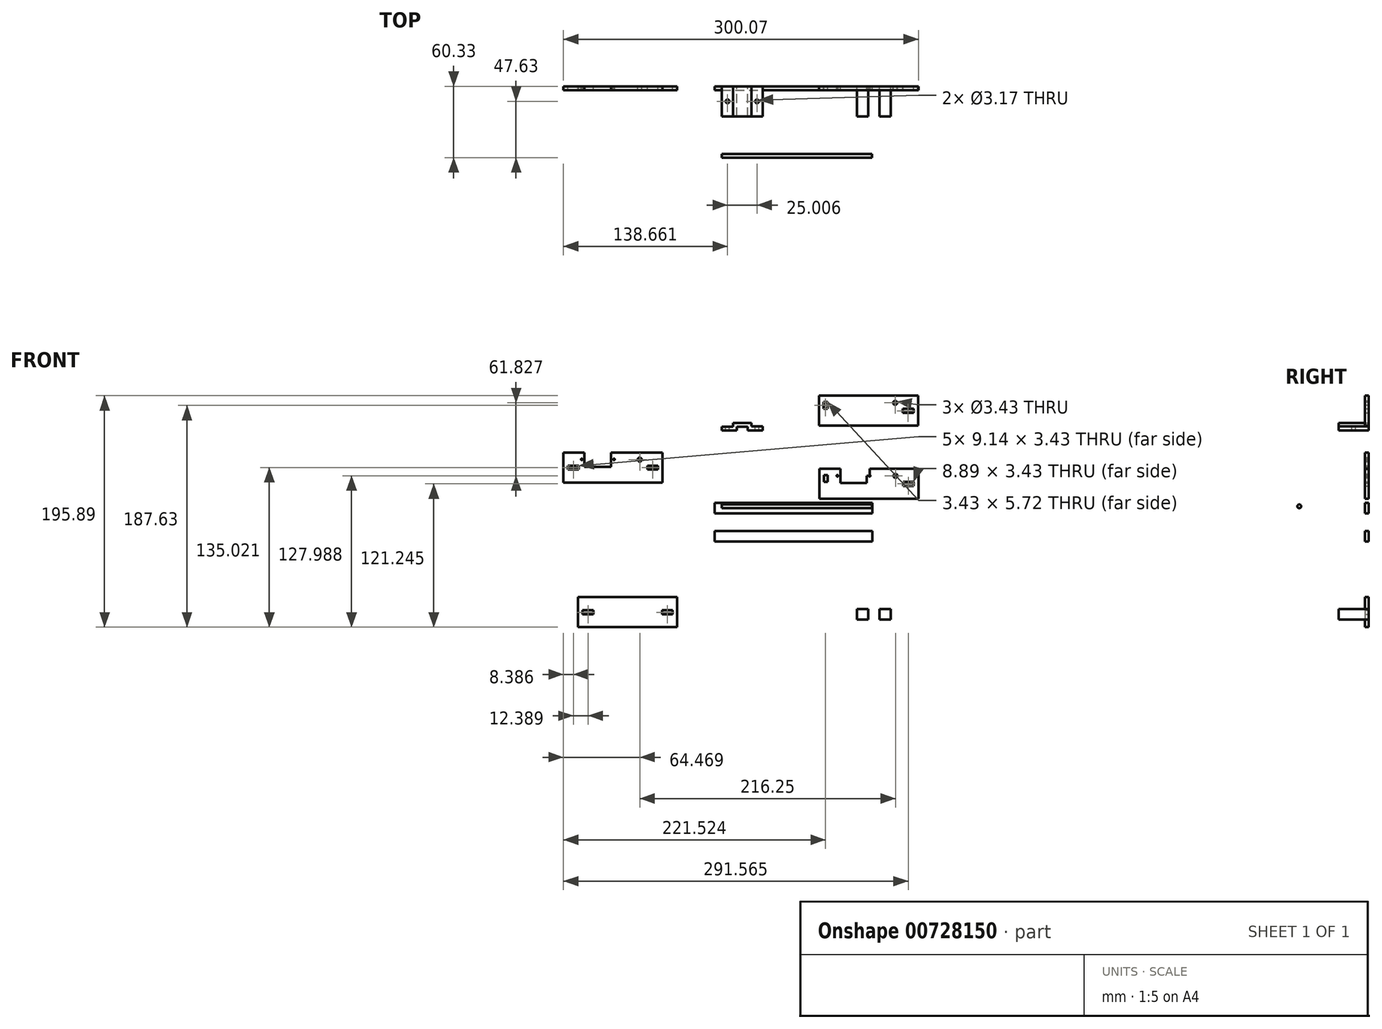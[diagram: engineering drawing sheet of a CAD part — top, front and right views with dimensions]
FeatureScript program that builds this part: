
annotation { "Feature Type Name" : "Feature", "Feature Type Description" : "" }
export const myFeature = defineFeature(function(context is Context, id is Id, definition is map)
    precondition{}
    {
        {
            var Q0;
            Q0=qCreatedBy(makeId("Front.planeOp"),FACE);
            var sketch = newSketch(context, id + "F0", { "sketchPlane" : qUnion([Q0])});
            skLineSegment(sketch, "E0.bottom", {"start": v(-44.59, 14.54) * mm, "end": v(39.23, 14.54) * mm});
            skLineSegment(sketch, "E0.top", {"start": v(-44.59, -10.86) * mm, "end": v(39.23, -10.86) * mm});
            skLineSegment(sketch, "E0.left", {"start": v(-44.59, 14.54) * mm, "end": v(-44.59, -10.86) * mm});
            skLineSegment(sketch, "E0.right", {"start": v(39.23, 14.54) * mm, "end": v(39.23, -10.86) * mm});
            skLineSegment(sketch, "E1.bottom", {"start": v(-28.47, -10.86) * mm, "end": v(-5.43, -10.86) * mm});
            skLineSegment(sketch, "E2.bottom", {"start": v(-133.06, -14.32) * mm, "end": v(0.29, -14.32) * mm});
            skLineSegment(sketch, "E2.top", {"start": v(-133.06, -23.21) * mm, "end": v(0.29, -23.21) * mm});
            skLineSegment(sketch, "E2.left", {"start": v(-133.06, -14.32) * mm, "end": v(-133.06, -23.21) * mm});
            skLineSegment(sketch, "E2.right", {"start": v(0.29, -14.32) * mm, "end": v(0.29, -23.21) * mm});
            skLineSegment(sketch, "E3.bottom", {"start": v(-133.06, -38.27) * mm, "end": v(0.29, -38.27) * mm});
            skLineSegment(sketch, "E3.top", {"start": v(-133.06, -47.16) * mm, "end": v(0.29, -47.16) * mm});
            skLineSegment(sketch, "E3.left", {"start": v(-133.06, -38.27) * mm, "end": v(-133.06, -47.16) * mm});
            skLineSegment(sketch, "E3.right", {"start": v(0.29, -38.27) * mm, "end": v(0.29, -47.16) * mm});
            skLineSegment(sketch, "E4.bottom", {"start": v(-44.84, 76.36) * mm, "end": v(38.98, 76.36) * mm});
            skLineSegment(sketch, "E4.top", {"start": v(-44.84, 50.96) * mm, "end": v(38.98, 50.96) * mm});
            skLineSegment(sketch, "E4.left", {"start": v(-44.84, 76.36) * mm, "end": v(-44.84, 50.96) * mm});
            skLineSegment(sketch, "E4.right", {"start": v(38.98, 76.36) * mm, "end": v(38.98, 50.96) * mm});
            skLineSegment(sketch, "E5", {"start": v(-40.78, 14.54) * mm, "end": v(-40.78, 3.43) * mm});
            skLineSegment(sketch, "E6", {"start": v(-41.03, 76.36) * mm, "end": v(-41.03, 65.24) * mm});
            skLineSegment(sketch, "E7.bottom", {"start": v(-40.78, 3.43) * mm, "end": v(-31.89, 3.43) * mm});
            skLineSegment(sketch, "E7.top", {"start": v(-40.78, 0) * mm, "end": v(-31.89, 0) * mm});
            skLineSegment(sketch, "E7.left", {"start": v(-40.78, 3.43) * mm, "end": v(-40.78, 0) * mm});
            skLineSegment(sketch, "E7.right", {"start": v(-31.89, 3.43) * mm, "end": v(-31.89, 0) * mm});
            skLineSegment(sketch, "E8.bottom", {"start": v(-41.03, 65.24) * mm, "end": v(-31.89, 65.24) * mm});
            skLineSegment(sketch, "E8.top", {"start": v(-41.03, 61.81) * mm, "end": v(-31.89, 61.81) * mm});
            skLineSegment(sketch, "E8.left", {"start": v(-41.03, 65.24) * mm, "end": v(-41.03, 61.81) * mm});
            skLineSegment(sketch, "E8.right", {"start": v(-31.89, 65.24) * mm, "end": v(-31.89, 61.81) * mm});
            skLineSegment(sketch, "E9.bottom", {"start": v(-44.84, 76.36) * mm, "end": v(-41.03, 76.36) * mm});
            skLineSegment(sketch, "E9.top", {"start": v(-44.84, 76.36) * mm, "end": v(-41.03, 76.36) * mm});
            skLineSegment(sketch, "E9.left", {"start": v(-44.84, 76.36) * mm, "end": v(-44.84, 76.36) * mm});
            skLineSegment(sketch, "E9.right", {"start": v(-41.03, 76.36) * mm, "end": v(-41.03, 76.36) * mm});
            skLineSegment(sketch, "E10", {"start": v(35.17, 76.36) * mm, "end": v(35.17, 65.24) * mm});
            skPoint(sketch, "E11.oppositeSnap0", {"position": v(-36.46, 61.81) * mm});
            skLineSegment(sketch, "E11.bottom", {"start": v(35.17, 65.24) * mm, "end": v(26.03, 65.24) * mm});
            skLineSegment(sketch, "E11.top", {"start": v(35.17, 61.81) * mm, "end": v(26.03, 61.81) * mm});
            skLineSegment(sketch, "E11.left", {"start": v(35.17, 65.24) * mm, "end": v(35.17, 61.81) * mm});
            skLineSegment(sketch, "E11.right", {"start": v(26.03, 65.24) * mm, "end": v(26.03, 61.81) * mm});
            skLineSegment(sketch, "E12.left", {"start": v(35.42, 0.25) * mm, "end": v(35.17, 0) * mm});
            skLineSegment(sketch, "E13", {"start": v(35.42, 0.25) * mm, "end": v(35.42, -10.86) * mm});
            skLineSegment(sketch, "E14.bottom", {"start": v(35.17, 0) * mm, "end": v(26.28, 0) * mm});
            skLineSegment(sketch, "E14.top", {"start": v(35.17, 3.43) * mm, "end": v(26.28, 3.43) * mm});
            skLineSegment(sketch, "E14.left", {"start": v(35.17, 0) * mm, "end": v(35.17, 3.43) * mm});
            skLineSegment(sketch, "E14.right", {"start": v(26.28, 0) * mm, "end": v(26.28, 3.43) * mm});
            skLineSegment(sketch, "E15.bottom", {"start": v(-26.8, 14.54) * mm, "end": v(-4.33, 14.54) * mm});
            skLineSegment(sketch, "E15.top", {"start": v(-26.8, 2.37) * mm, "end": v(-4.33, 2.37) * mm});
            skLineSegment(sketch, "E15.left", {"start": v(-26.8, 14.54) * mm, "end": v(-26.8, 2.37) * mm});
            skLineSegment(sketch, "E15.right", {"start": v(-4.33, 14.54) * mm, "end": v(-4.33, 2.37) * mm});
            skLineSegment(sketch, "E16", {"start": v(-15.57, 14.54) * mm, "end": v(9.83, 14.54) * mm});
            skLineSegment(sketch, "E17", {"start": v(-44.84, 76.36) * mm, "end": v(9.6, 76.36) * mm});
            skLineSegment(sketch, "E18.bottom", {"start": v(-126.95, 53.3) * mm, "end": v(-92.41, 53.3) * mm});
            skLineSegment(sketch, "E18.top", {"start": v(-126.95, 46.96) * mm, "end": v(-92.41, 46.96) * mm});
            skLineSegment(sketch, "E18.left", {"start": v(-126.95, 53.3) * mm, "end": v(-126.95, 46.96) * mm});
            skLineSegment(sketch, "E18.right", {"start": v(-92.41, 53.3) * mm, "end": v(-92.41, 46.96) * mm});
            skLineSegment(sketch, "E19", {"start": v(-114.25, 46.96) * mm, "end": v(-114.25, 50.13) * mm});
            skLineSegment(sketch, "E20", {"start": v(-114.25, 50.13) * mm, "end": v(-105.11, 50.13) * mm});
            skLineSegment(sketch, "E21", {"start": v(-105.11, 50.13) * mm, "end": v(-105.11, 46.96) * mm});
            skLineSegment(sketch, "E22", {"start": v(-126.95, 50.13) * mm, "end": v(-117.43, 50.13) * mm});
            skLineSegment(sketch, "E23", {"start": v(-117.43, 50.13) * mm, "end": v(-117.43, 53.3) * mm});
            skLineSegment(sketch, "E24", {"start": v(-101.94, 53.3) * mm, "end": v(-101.94, 50.36) * mm});
            skLineSegment(sketch, "E25", {"start": v(-101.94, 50.36) * mm, "end": v(-92.41, 50.36) * mm});
            skLineSegment(sketch, "E26", {"start": v(-29.19, 14.54) * mm, "end": v(-29.19, 8.6) * mm});
            skLineSegment(sketch, "E27", {"start": v(-29.19, 8.6) * mm, "end": v(-26.8, 8.6) * mm});
            skLineSegment(sketch, "E28.bottom", {"start": v(-4.33, 14.54) * mm, "end": v(-1.94, 14.54) * mm});
            skLineSegment(sketch, "E28.left", {"start": v(-4.33, 14.54) * mm, "end": v(-4.33, 8.59) * mm});
            skLineSegment(sketch, "E28.right", {"start": v(-1.94, 14.54) * mm, "end": v(-1.94, 8.59) * mm});
            skCircle(sketch, "E29", {"center": v(-29.19, 8.6) * mm, "radius": 0.64 * mm});
            skCircle(sketch, "E30", {"center": v(-1.94, 8.59) * mm, "radius": 0.64 * mm});
            skLineSegment(sketch, "E31.bottom", {"start": v(-260.84, 28.33) * mm, "end": v(-177.02, 28.33) * mm});
            skLineSegment(sketch, "E31.top", {"start": v(-260.84, 2.93) * mm, "end": v(-177.02, 2.93) * mm});
            skLineSegment(sketch, "E31.left", {"start": v(-260.84, 28.33) * mm, "end": v(-260.84, 2.93) * mm});
            skLineSegment(sketch, "E31.right", {"start": v(-177.02, 28.33) * mm, "end": v(-177.02, 2.93) * mm});
            skLineSegment(sketch, "E32", {"start": v(-257.03, 28.33) * mm, "end": v(-180.83, 28.33) * mm});
            skLineSegment(sketch, "E33.bottom", {"start": v(-257.03, 17.2) * mm, "end": v(-247.88, 17.2) * mm});
            skLineSegment(sketch, "E33.top", {"start": v(-257.03, 13.78) * mm, "end": v(-247.88, 13.78) * mm});
            skLineSegment(sketch, "E33.left", {"start": v(-257.03, 17.2) * mm, "end": v(-257.03, 13.78) * mm});
            skLineSegment(sketch, "E33.right", {"start": v(-247.88, 17.2) * mm, "end": v(-247.88, 13.78) * mm});
            skLineSegment(sketch, "E34.bottom", {"start": v(-180.83, 17.2) * mm, "end": v(-189.97, 17.2) * mm});
            skLineSegment(sketch, "E34.top", {"start": v(-180.83, 13.78) * mm, "end": v(-189.97, 13.78) * mm});
            skLineSegment(sketch, "E34.left", {"start": v(-180.83, 17.2) * mm, "end": v(-180.83, 13.78) * mm});
            skLineSegment(sketch, "E34.right", {"start": v(-189.97, 17.2) * mm, "end": v(-189.97, 13.78) * mm});
            skLineSegment(sketch, "E35", {"start": v(-10.6, 8.46) * mm, "end": v(19.88, 8.46) * mm});
            skLineSegment(sketch, "E36", {"start": v(9.6, 76.36) * mm, "end": v(9.6, 70.26) * mm});
            skLineSegment(sketch, "E37.bottom", {"start": v(-260.84, 28.33) * mm, "end": v(-206.4, 28.33) * mm});
            skLineSegment(sketch, "E37.left", {"start": v(-260.84, 28.33) * mm, "end": v(-260.84, 22.23) * mm});
            skLineSegment(sketch, "E38", {"start": v(-260.84, 28.33) * mm, "end": v(-243.06, 28.33) * mm});
            skLineSegment(sketch, "E39.bottom", {"start": v(-243.06, 28.33) * mm, "end": v(-220.58, 28.33) * mm});
            skLineSegment(sketch, "E39.top", {"start": v(-243.06, 16.16) * mm, "end": v(-220.58, 16.16) * mm});
            skLineSegment(sketch, "E39.left", {"start": v(-243.06, 28.33) * mm, "end": v(-243.06, 16.16) * mm});
            skLineSegment(sketch, "E39.right", {"start": v(-220.58, 28.33) * mm, "end": v(-220.58, 16.16) * mm});
            skCircle(sketch, "E40", {"center": v(-245.44, 22.39) * mm, "radius": 0.64 * mm});
            skCircle(sketch, "E41", {"center": v(-218.19, 22.39) * mm, "radius": 0.64 * mm});
            skLineSegment(sketch, "E42.bottom", {"start": v(-248.45, -94.13) * mm, "end": v(-164.63, -94.13) * mm});
            skLineSegment(sketch, "E42.top", {"start": v(-248.45, -119.53) * mm, "end": v(-164.63, -119.53) * mm});
            skLineSegment(sketch, "E42.left", {"start": v(-248.45, -94.13) * mm, "end": v(-248.45, -119.53) * mm});
            skLineSegment(sketch, "E42.right", {"start": v(-164.63, -94.13) * mm, "end": v(-164.63, -119.53) * mm});
            skLineSegment(sketch, "E43", {"start": v(-248.45, -94.13) * mm, "end": v(-244.64, -94.13) * mm});
            skLineSegment(sketch, "E44", {"start": v(-164.63, -94.13) * mm, "end": v(-168.44, -94.13) * mm});
            skLineSegment(sketch, "E45", {"start": v(-244.64, -94.13) * mm, "end": v(-244.64, -105.25) * mm});
            skLineSegment(sketch, "E46", {"start": v(-168.44, -94.13) * mm, "end": v(-168.44, -105.25) * mm});
            skLineSegment(sketch, "E47.bottom", {"start": v(-244.64, -105.25) * mm, "end": v(-235.5, -105.25) * mm});
            skLineSegment(sketch, "E47.top", {"start": v(-244.64, -108.68) * mm, "end": v(-235.5, -108.68) * mm});
            skLineSegment(sketch, "E47.left", {"start": v(-244.64, -105.25) * mm, "end": v(-244.64, -108.68) * mm});
            skLineSegment(sketch, "E47.right", {"start": v(-235.5, -105.25) * mm, "end": v(-235.5, -108.68) * mm});
            skLineSegment(sketch, "E48.bottom", {"start": v(-168.44, -105.25) * mm, "end": v(-177.58, -105.25) * mm});
            skLineSegment(sketch, "E48.top", {"start": v(-168.44, -108.68) * mm, "end": v(-177.58, -108.68) * mm});
            skLineSegment(sketch, "E48.left", {"start": v(-168.44, -105.25) * mm, "end": v(-168.44, -108.68) * mm});
            skLineSegment(sketch, "E48.right", {"start": v(-177.58, -105.25) * mm, "end": v(-177.58, -108.68) * mm});
            skLineSegment(sketch, "E49.bottom", {"start": v(-98.52, -99.6) * mm, "end": v(-63.97, -99.6) * mm});
            skLineSegment(sketch, "E49.top", {"start": v(-98.52, -106.2) * mm, "end": v(-63.97, -106.2) * mm});
            skLineSegment(sketch, "E49.left", {"start": v(-98.52, -99.6) * mm, "end": v(-98.52, -106.2) * mm});
            skLineSegment(sketch, "E49.right", {"start": v(-63.97, -99.6) * mm, "end": v(-63.97, -106.2) * mm});
            skLineSegment(sketch, "E50.bottom", {"start": v(-98.52, -99.6) * mm, "end": v(-89, -99.6) * mm});
            skLineSegment(sketch, "E50.top", {"start": v(-98.52, -97.05) * mm, "end": v(-89, -97.05) * mm});
            skLineSegment(sketch, "E50.left", {"start": v(-98.52, -97.05) * mm, "end": v(-98.52, -99.6) * mm});
            skLineSegment(sketch, "E50.right", {"start": v(-89, -97.05) * mm, "end": v(-89, -99.6) * mm});
            skLineSegment(sketch, "E51.bottom", {"start": v(-63.97, -99.6) * mm, "end": v(-73.5, -99.6) * mm});
            skLineSegment(sketch, "E51.top", {"start": v(-63.97, -102.77) * mm, "end": v(-73.5, -102.77) * mm});
            skLineSegment(sketch, "E51.left", {"start": v(-63.97, -99.6) * mm, "end": v(-63.97, -102.77) * mm});
            skLineSegment(sketch, "E51.right", {"start": v(-73.5, -99.6) * mm, "end": v(-73.5, -102.77) * mm});
            skLineSegment(sketch, "E52.bottom", {"start": v(-85.82, -106.2) * mm, "end": v(-76.67, -106.2) * mm});
            skLineSegment(sketch, "E52.top", {"start": v(-85.82, -97.05) * mm, "end": v(-76.67, -97.05) * mm});
            skLineSegment(sketch, "E52.left", {"start": v(-85.82, -106.2) * mm, "end": v(-85.82, -97.05) * mm});
            skLineSegment(sketch, "E52.right", {"start": v(-76.67, -106.2) * mm, "end": v(-76.67, -97.05) * mm});
            skLineSegment(sketch, "E53", {"start": v(-10.6, 14.54) * mm, "end": v(-4.33, 14.54) * mm});
            skLineSegment(sketch, "E54", {"start": v(-10.6, 14.54) * mm, "end": v(-10.6, 8.46) * mm});
            skCircle(sketch, "E55", {"center": v(19.88, 8.46) * mm, "radius": 1.71 * mm});
            skLineSegment(sketch, "E56", {"start": v(-226.85, 28.33) * mm, "end": v(-220.58, 28.33) * mm});
            skCircle(sketch, "E57", {"center": v(-196.37, 22.23) * mm, "radius": 1.71 * mm});
            skLineSegment(sketch, "E58.bottom", {"start": v(35.17, 61.81) * mm, "end": v(31.74, 61.81) * mm});
            skLineSegment(sketch, "E58.top", {"start": v(35.17, 70.96) * mm, "end": v(31.74, 70.96) * mm});
            skLineSegment(sketch, "E58.left", {"start": v(35.17, 61.81) * mm, "end": v(35.17, 70.96) * mm});
            skLineSegment(sketch, "E58.right", {"start": v(31.74, 61.81) * mm, "end": v(31.74, 70.96) * mm});
            skLineSegment(sketch, "E59.bottom", {"start": v(-12.7, -104.07) * mm, "end": v(15.88, -104.07) * mm});
            skLineSegment(sketch, "E59.top", {"start": v(-12.7, -116.14) * mm, "end": v(15.88, -116.14) * mm});
            skLineSegment(sketch, "E59.left", {"start": v(-12.7, -104.07) * mm, "end": v(-12.7, -116.14) * mm});
            skLineSegment(sketch, "E59.right", {"start": v(15.88, -104.07) * mm, "end": v(15.88, -116.14) * mm});
            skLineSegment(sketch, "E60.bottom", {"start": v(15.93, -104.07) * mm, "end": v(15.88, -104.07) * mm});
            skLineSegment(sketch, "E60.top", {"start": v(15.91, -101) * mm, "end": v(15.88, -101) * mm});
            skLineSegment(sketch, "E61.bottom", {"start": v(0, -116.14) * mm, "end": v(3.18, -116.14) * mm});
            skLineSegment(sketch, "E61.top", {"start": v(0, -107.25) * mm, "end": v(3.17, -107.25) * mm});
            skLineSegment(sketch, "E61.left", {"start": v(0, -116.14) * mm, "end": v(0, -107.25) * mm});
            skLineSegment(sketch, "E61.right", {"start": v(3.18, -116.14) * mm, "end": v(3.17, -107.25) * mm});
            skLineSegment(sketch, "E62.bottom", {"start": v(-12.7, -104.07) * mm, "end": v(-3.18, -104.07) * mm});
            skLineSegment(sketch, "E62.top", {"start": v(-12.7, -112.96) * mm, "end": v(-3.18, -112.96) * mm});
            skLineSegment(sketch, "E62.left", {"start": v(-12.7, -104.07) * mm, "end": v(-12.7, -112.96) * mm});
            skLineSegment(sketch, "E62.right", {"start": v(-3.18, -104.07) * mm, "end": v(-3.18, -112.96) * mm});
            skLineSegment(sketch, "E63.bottom", {"start": v(15.93, -104.07) * mm, "end": v(6.4, -104.07) * mm});
            skLineSegment(sketch, "E63.top", {"start": v(15.93, -112.97) * mm, "end": v(6.4, -112.97) * mm});
            skLineSegment(sketch, "E63.left", {"start": v(15.93, -104.07) * mm, "end": v(15.93, -112.97) * mm});
            skLineSegment(sketch, "E63.right", {"start": v(6.4, -104.07) * mm, "end": v(6.4, -112.97) * mm});
            skLineSegment(sketch, "E64", {"start": v(-44.84, 76.36) * mm, "end": v(19.62, 76.36) * mm});
            skLineSegment(sketch, "E65", {"start": v(19.62, 76.36) * mm, "end": v(19.62, 70.28) * mm});
            skCircle(sketch, "E66", {"center": v(19.62, 70.28) * mm, "radius": 1.71 * mm});
            skLineSegment(sketch, "E67.bottom", {"start": v(-40.78, 0) * mm, "end": v(-37.35, 0) * mm});
            skLineSegment(sketch, "E67.top", {"start": v(-40.78, 9.14) * mm, "end": v(-37.35, 9.14) * mm});
            skLineSegment(sketch, "E67.left", {"start": v(-40.78, 0) * mm, "end": v(-40.78, 9.14) * mm});
            skLineSegment(sketch, "E67.right", {"start": v(-37.35, 0) * mm, "end": v(-37.35, 9.14) * mm});
            skLineSegment(sketch, "E68.bottom", {"start": v(-41.03, 61.81) * mm, "end": v(-37.6, 61.81) * mm});
            skLineSegment(sketch, "E68.top", {"start": v(-41.03, 70.96) * mm, "end": v(-37.6, 70.96) * mm});
            skLineSegment(sketch, "E68.left", {"start": v(-41.03, 61.81) * mm, "end": v(-41.03, 70.96) * mm});
            skLineSegment(sketch, "E68.right", {"start": v(-37.6, 61.81) * mm, "end": v(-37.6, 70.96) * mm});
            skSolve(sketch);
        }
        {
            var Q0;
            Q0=makeQuery(id+"F0.imprint","IMPRINT",FACE,{"disambiguationData":[TD([[makeQuery(id+"F0.imprint","IMPRINT",EDGE,{"derivedFrom":sQuery(id+"F0.wireOp",EDGE,"E2.bottom")}),-1.0]])]});
            extrude(context, id + "F1", {"entities" : qUnion([Q0]), "depth" : 3.17 * mm, "offsetDistance" : 25.4 * mm});
        }
        {
            var Q0;
            Q0=makeQuery(id+"F0.imprint","IMPRINT",FACE,{"disambiguationData":[TD([[makeQuery(id+"F0.imprint","IMPRINT",EDGE,{"derivedFrom":sQuery(id+"F0.wireOp",EDGE,"E3.bottom")}),-1.0]])]});
            extrude(context, id + "F2", {"entities" : qUnion([Q0]), "depth" : 3.17 * mm, "offsetDistance" : 25.4 * mm});
        }
        {
            var Q0;
            Q0=makeQuery(id+"F0.imprint","IMPRINT",FACE,{"disambiguationData":[TD([[makeQuery(id+"F0.imprint","IMPRINT",EDGE,{"derivedFrom":sQuery(id+"F0.wireOp",EDGE,"E4.bottom")}),-1.0]])]});
            var Q1;
            {var subQ4=sQuery(id+"F0.wireOp",EDGE,"E8.top");Q1=makeQuery(id+"F0.imprint","IMPRINT",FACE,{"disambiguationData":[TD([[makeQuery(id+"F0.imprint","IMPRINT",EDGE,{"derivedFrom":subQ4}),1.0]])]});}
            var Q2;
            {var subQ5=sQuery(id+"F0.wireOp",EDGE,"E58.top");Q2=makeQuery(id+"F0.imprint","IMPRINT",FACE,{"disambiguationData":[TD([[makeQuery(id+"F0.imprint","IMPRINT",EDGE,{"derivedFrom":subQ5}),1.0]])]});}
            extrude(context, id + "F3", {"entities" : qUnion([Q0, Q1, Q2]), "depth" : 3.17 * mm, "offsetDistance" : 25.4 * mm});
        }
        {
            var Q0;
            {var subQ3=sQuery(id+"F0.wireOp",EDGE,"E0.left");Q0=makeQuery(id+"F0.imprint","IMPRINT",FACE,{"disambiguationData":[TD([[makeQuery(id+"F0.imprint","IMPRINT",EDGE,{"derivedFrom":subQ3}),1.0]])]});}
            var Q1;
            {var subQ5=sQuery(id+"F0.wireOp",EDGE,"E0.bottom");var subQ7=sQuery(id+"F0.wireOp",EDGE,"E26");var subQ8=makeQuery(id+"F0.imprint","INTERSECT",VERTEX,{"derivedFrom":[subQ5,subQ7]});Q1=makeQuery(id+"F0.imprint","IMPRINT",FACE,{"disambiguationData":[TD([[makeQuery(id+"F0.imprint","IMPRINT",EDGE,{"disambiguationData":[TD([[subQ8,-1.0]])],"derivedFrom":subQ7}),1.0]])]});}
            var Q2;
            {var subQ1=sQuery(id+"F0.wireOp",EDGE,"E28.bottom");Q2=makeQuery(id+"F0.imprint","IMPRINT",FACE,{"disambiguationData":[TD([[makeQuery(id+"F0.imprint","IMPRINT",EDGE,{"derivedFrom":subQ1}),-1.0]])]});}
            var Q3;
            {var subQ4=sQuery(id+"F0.wireOp",EDGE,"E7.top");Q3=makeQuery(id+"F0.imprint","IMPRINT",FACE,{"disambiguationData":[TD([[makeQuery(id+"F0.imprint","IMPRINT",EDGE,{"derivedFrom":subQ4}),1.0]])]});}
            extrude(context, id + "F4", {"entities" : qUnion([Q0, Q1, Q2, Q3]), "depth" : 3.17 * mm, "offsetDistance" : 25.4 * mm});
        }
        {
            var Q0;
            {var subQ1=sQuery(id+"F0.wireOp",EDGE,"E19");Q0=makeQuery(id+"F0.imprint","IMPRINT",FACE,{"disambiguationData":[TD([[makeQuery(id+"F0.imprint","IMPRINT",EDGE,{"derivedFrom":subQ1}),1.0]])]});}
            extrude(context, id + "F5", {"entities" : qUnion([Q0]), "depth" : 25.4 * mm, "offsetDistance" : 25.4 * mm});
        }
        {
            var Q0;
            Q0=makeQuery(id+"F5.opExtrude","SWEPT_FACE",FACE,{"disambiguationData":[OSD([sQuery(id+"F0.wireOp",EDGE,"E25")])]});
            var sketch = newSketch(context, id + "F6", { "sketchPlane" : qUnion([Q0])});
            skLineSegment(sketch, "E69", {"start": v(-92.41, -12.7) * mm, "end": v(-97.17, -12.7) * mm});
            skCircle(sketch, "E70", {"center": v(-97.17, -12.7) * mm, "radius": 1.59 * mm});
            skSolve(sketch);
        }
        {
            var Q0;
            Q0=makeQuery(id+"F5.opExtrude","SWEPT_FACE",FACE,{"disambiguationData":[OSD([sQuery(id+"F0.wireOp",EDGE,"E22")])]});
            var sketch = newSketch(context, id + "F7", { "sketchPlane" : qUnion([Q0])});
            skLineSegment(sketch, "E71", {"start": v(-126.95, -12.7) * mm, "end": v(-122.18, -12.7) * mm});
            skCircle(sketch, "E72", {"center": v(-122.18, -12.7) * mm, "radius": 1.59 * mm});
            skSolve(sketch);
        }
        {
            var Q0;
            Q0=makeQuery(id+"F7.imprint","IMPRINT",FACE,{"disambiguationData":[TD([[makeQuery(id+"F7.imprint","IMPRINT",EDGE,{"derivedFrom":sQuery(id+"F7.wireOp",EDGE,"E72")}),1.0]])]});
            var Q1;
            Q1=makeQuery(id+"F6.imprint","IMPRINT",FACE,{"disambiguationData":[TD([[makeQuery(id+"F6.imprint","IMPRINT",EDGE,{"derivedFrom":sQuery(id+"F6.wireOp",EDGE,"E70")}),1.0]])]});
            extrude(context, id + "F8", {"entities" : qUnion([Q0, Q1]), "operationType" : NewBodyOperationType.REMOVE, "endBound" : BoundingType.THROUGH_ALL, "oppositeDirection" : true, "depth" : 25.4 * mm, "offsetDistance" : 25.4 * mm});
        }
        {
            var Q0;
            {var subQ5=sQuery(id+"F0.wireOp",EDGE,"E37.left");Q0=makeQuery(id+"F0.imprint","IMPRINT",FACE,{"disambiguationData":[TD([[makeQuery(id+"F0.imprint","IMPRINT",EDGE,{"derivedFrom":subQ5}),1.0]])]});}
            var Q1;
            {var subQ1=sQuery(id+"F0.wireOp",EDGE,"E38");var subQ5=sQuery(id+"F0.wireOp",EDGE,"6emhHhDK-PmYR-VBVO-gdcs-AIFIT5EJHPEa");var subQ6=makeQuery(id+"F0.imprint","INTERSECT",VERTEX,{"derivedFrom":[subQ5,subQ1]});Q1=makeQuery(id+"F0.imprint","IMPRINT",FACE,{"disambiguationData":[TD([[makeQuery(id+"F0.imprint","IMPRINT",EDGE,{"disambiguationData":[TD([[subQ6,-1.0]])],"derivedFrom":subQ5}),1.0]])]});}
            var Q2;
            {var subQ3=sQuery(id+"F0.wireOp",EDGE,"E37.top");var subQ7=sQuery(id+"F0.wireOp",EDGE,"E40");var subQ9=makeQuery(id+"F0.imprint","INTERSECT",VERTEX,{"disambiguationData":[OD(1.0)],"derivedFrom":[subQ3,subQ7]});Q2=makeQuery(id+"F0.imprint","IMPRINT",FACE,{"disambiguationData":[TD([[makeQuery(id+"F0.imprint","IMPRINT",EDGE,{"disambiguationData":[TD([[subQ9,-1.0]])],"derivedFrom":subQ3}),1.0]])]});}
            var Q3;
            {var subQ0=sQuery(id+"F0.wireOp",EDGE,"E33.bottom");Q3=makeQuery(id+"F0.imprint","IMPRINT",FACE,{"disambiguationData":[TD([[makeQuery(id+"F0.imprint","IMPRINT",EDGE,{"derivedFrom":subQ0}),1.0]])]});}
            var Q4;
            Q4=makeQuery(id+"F0.imprint","IMPRINT",FACE,{"disambiguationData":[TD([[makeQuery(id+"F0.imprint","IMPRINT",EDGE,{"derivedFrom":sQuery(id+"F0.wireOp",EDGE,"E31.bottom")}),-1.0]])]});
            var Q5;
            {var subQ7=sQuery(id+"F0.wireOp",EDGE,"E41");var subQ9=sQuery(id+"F0.wireOp",EDGE,"E37.top");var subQ10=makeQuery(id+"F0.imprint","INTERSECT",VERTEX,{"disambiguationData":[OD(1.0)],"derivedFrom":[subQ9,subQ7]});Q5=makeQuery(id+"F0.imprint","IMPRINT",FACE,{"disambiguationData":[TD([[makeQuery(id+"F0.imprint","IMPRINT",EDGE,{"disambiguationData":[TD([[subQ10,-1.0]])],"derivedFrom":subQ9}),1.0]])]});}
            var Q6;
            {var subQ0=sQuery(id+"F0.wireOp",EDGE,"E39.right");var subQ3=sQuery(id+"F0.wireOp",EDGE,"E37.top");var subQ4=makeQuery(id+"F0.imprint","INTERSECT",VERTEX,{"derivedFrom":[subQ3,subQ0]});Q6=makeQuery(id+"F0.imprint","IMPRINT",FACE,{"disambiguationData":[TD([[makeQuery(id+"F0.imprint","IMPRINT",EDGE,{"disambiguationData":[TD([[subQ4,-1.0]])],"derivedFrom":subQ3}),1.0]])]});}
            var Q7;
            {var subQ1=sQuery(id+"F0.wireOp",EDGE,"1SVwMFwp-ebtT-SsTF-cnTG-4ujLHmDgcyX8");var subQ6=sQuery(id+"F0.wireOp",EDGE,"E37.bottom");var subQ8=makeQuery(id+"F0.imprint","INTERSECT",VERTEX,{"derivedFrom":[subQ6,subQ1]});Q7=makeQuery(id+"F0.imprint","IMPRINT",FACE,{"disambiguationData":[TD([[makeQuery(id+"F0.imprint","IMPRINT",EDGE,{"disambiguationData":[TD([[subQ8,-1.0]])],"derivedFrom":subQ1}),-1.0]])]});}
            var Q8;
            {var subQ7=sQuery(id+"F0.wireOp",EDGE,"E37.right");Q8=makeQuery(id+"F0.imprint","IMPRINT",FACE,{"disambiguationData":[TD([[makeQuery(id+"F0.imprint","IMPRINT",EDGE,{"derivedFrom":subQ7}),-1.0]])]});}
            extrude(context, id + "F9", {"entities" : qUnion([Q0, Q1, Q2, Q3, Q4, Q5, Q6, Q7, Q8]), "depth" : 3.17 * mm, "offsetDistance" : 25.4 * mm});
        }
        {
            var Q0;
            Q0=makeQuery(id+"F0.imprint","IMPRINT",FACE,{"disambiguationData":[TD([[makeQuery(id+"F0.imprint","IMPRINT",EDGE,{"derivedFrom":sQuery(id+"F0.wireOp",EDGE,"E42.bottom")}),-1.0]])]});
            extrude(context, id + "F10", {"entities" : qUnion([Q0]), "depth" : 3.17 * mm, "offsetDistance" : 25.4 * mm});
        }
        {
            var Q0;
            Q0=qCreatedBy(makeId("Right.planeOp"),FACE);
            var sketch = newSketch(context, id + "F11", { "sketchPlane" : qUnion([Q0])});
            skCircle(sketch, "E73", {"center": v(-58.74, -17.27) * mm, "radius": 1.59 * mm});
            skSolve(sketch);
        }
        {
            var Q0;
            Q0=makeQuery(id+"F11.imprint","IMPRINT",FACE,{"disambiguationData":[TD([[makeQuery(id+"F11.imprint","IMPRINT",EDGE,{"derivedFrom":sQuery(id+"F11.wireOp",EDGE,"E73")}),1.0]])]});
            extrude(context, id + "F12", {"entities" : qUnion([Q0]), "oppositeDirection" : true, "depth" : 127 * mm, "offsetDistance" : 25.4 * mm});
        }
        {
            var Q0;
            Q0=makeQuery(id+"F0.imprint","IMPRINT",FACE,{"disambiguationData":[TD([[makeQuery(id+"F0.imprint","IMPRINT",EDGE,{"derivedFrom":sQuery(id+"F0.wireOp",EDGE,"E59.bottom")}),-1.0]])]});
            extrude(context, id + "F13", {"entities" : qUnion([Q0]), "depth" : 25.4 * mm, "offsetDistance" : 25.4 * mm});
        }
        {
            var Q0;
            Q0=makeQuery(id+"F13.opExtrude","SWEPT_FACE",FACE,{"disambiguationData":[OSD([sQuery(id+"F0.wireOp",EDGE,"E62.top")])]});
            var sketch = newSketch(context, id + "F14", { "sketchPlane" : qUnion([Q0])});
            skLineSegment(sketch, "E74", {"start": v(-12.7, -12.7) * mm, "end": v(-7.94, -12.7) * mm});
            skLineSegment(sketch, "E75", {"start": v(-7.94, -25.4) * mm, "end": v(-7.94, -3.56) * mm});
            skCircle(sketch, "E76", {"center": v(-7.94, -12.7) * mm, "radius": 1.59 * mm});
            skSolve(sketch);
        }
        {
            var Q0;
            Q0=makeQuery(id+"F13.opExtrude","SWEPT_FACE",FACE,{"disambiguationData":[OSD([sQuery(id+"F0.wireOp",EDGE,"E63.top")])]});
            var sketch = newSketch(context, id + "F15", { "sketchPlane" : qUnion([Q0])});
            skLineSegment(sketch, "E77", {"start": v(6.4, -12.7) * mm, "end": v(11.14, -12.7) * mm});
            skPoint(sketch, "E77.endSnap0", {"position": v(11.14, -25.4) * mm});
            skCircle(sketch, "E78", {"center": v(11.14, -12.7) * mm, "radius": 1.59 * mm});
            skSolve(sketch);
        }
        {
            var Q0;
            {var subQ0=sQuery(id+"F14.wireOp",EDGE,"E75");var subQ1=makeQuery(id+"F14.imprint","INTERSECT",VERTEX,{"derivedFrom":[sQuery(id+"F14.wireOp",EDGE,"E74"),subQ0]});Q0=makeQuery(id+"F14.imprint","IMPRINT",FACE,{"disambiguationData":[TD([[makeQuery(id+"F14.imprint","IMPRINT",EDGE,{"disambiguationData":[TD([[subQ1,1.0]])],"derivedFrom":subQ0}),-1.0]])]});}
            var Q1;
            {var subQ0=sQuery(id+"F14.wireOp",EDGE,"E75");var subQ1=sQuery(id+"F14.wireOp",EDGE,"E74");var subQ2=makeQuery(id+"F14.imprint","INTERSECT",VERTEX,{"derivedFrom":[subQ1,subQ0]});Q1=makeQuery(id+"F14.imprint","IMPRINT",FACE,{"disambiguationData":[TD([[makeQuery(id+"F14.imprint","IMPRINT",EDGE,{"disambiguationData":[TD([[subQ2,1.0]])],"derivedFrom":subQ1}),-1.0]])]});}
            var Q2;
            {var subQ0=sQuery(id+"F14.wireOp",EDGE,"E75");var subQ1=sQuery(id+"F14.wireOp",EDGE,"E74");var subQ2=makeQuery(id+"F14.imprint","INTERSECT",VERTEX,{"derivedFrom":[subQ1,subQ0]});Q2=makeQuery(id+"F14.imprint","IMPRINT",FACE,{"disambiguationData":[TD([[makeQuery(id+"F14.imprint","IMPRINT",EDGE,{"disambiguationData":[TD([[subQ2,1.0]])],"derivedFrom":subQ1}),1.0]])]});}
            var Q3;
            Q3=makeQuery(id+"F15.imprint","IMPRINT",FACE,{"disambiguationData":[TD([[makeQuery(id+"F15.imprint","IMPRINT",EDGE,{"derivedFrom":sQuery(id+"F15.wireOp",EDGE,"E78")}),1.0]])]});
            extrude(context, id + "F16", {"entities" : qUnion([Q0, Q1, Q2, Q3]), "operationType" : NewBodyOperationType.REMOVE, "endBound" : BoundingType.THROUGH_ALL, "oppositeDirection" : true, "depth" : 25.4 * mm, "offsetDistance" : 25.4 * mm});
        }
    });
